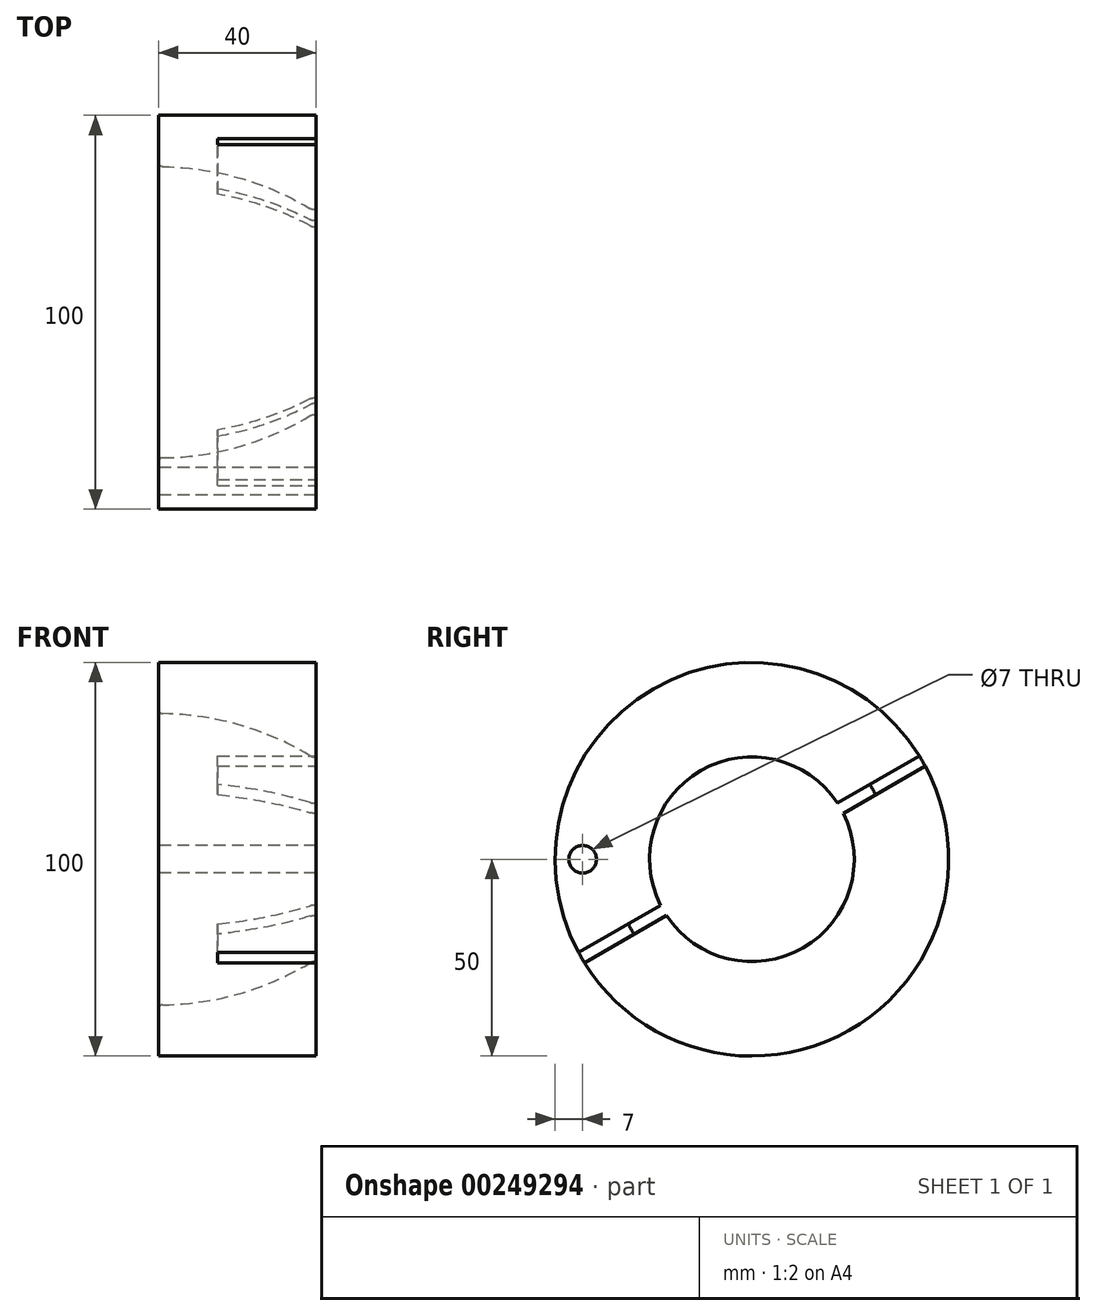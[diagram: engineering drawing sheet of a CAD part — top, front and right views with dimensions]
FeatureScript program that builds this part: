
annotation { "Feature Type Name" : "Feature", "Feature Type Description" : "" }
export const myFeature = defineFeature(function(context is Context, id is Id, definition is map)
    precondition{}
    {
        {
            var Q0;
            Q0=qCreatedBy(makeId("Front.planeOp"),FACE);
            var sketch = newSketch(context, id + "F0", { "sketchPlane" : qUnion([Q0])});
            skLineSegment(sketch, "E0", {"start": v(0, 50) * mm, "end": v(40, 50) * mm});
            skLineSegment(sketch, "E1", {"start": v(0, 0) * mm, "end": v(-40.59, 0) * mm, "construction": true});
            skLineSegment(sketch, "E2", {"start": v(40, 50) * mm, "end": v(40, 26) * mm});
            skLineSegment(sketch, "E3", {"start": v(40, 26) * mm, "end": v(39, 26) * mm});
            skLineSegment(sketch, "E4", {"start": v(0, 50) * mm, "end": v(0, 37) * mm});
            skArc(sketch, "E5", {"start": v(39, 26) * mm, "mid": v(20.26, 34.2) * mm, "end": v(0, 37) * mm});
            skSolve(sketch);
        }
        {
            var Q0;
            Q0=makeQuery(id+"F0.imprint","IMPRINT",FACE,{"disambiguationData":[TD([[makeQuery(id+"F0.imprint","IMPRINT",EDGE,{"derivedFrom":sQuery(id+"F0.wireOp",EDGE,"E0")}),-1.0]])]});
            var Q1;
            Q1=sQuery(id+"F0.wireOp",EDGE,"E1");
            revolve(context, id + "F1", {"surfaceOperationType" : NewSurfaceOperationType.NEW, "entities" : qUnion([Q0]), "axis" : qUnion([Q1]), "revolveType" : RevolveType.FULL});
        }
        {
            var Q0;
            Q0=makeQuery(id+"F1.opRevolve","SWEPT_EDGE",EDGE,{"disambiguationData":[OSD([sQuery(id+"F0.wireOp",EDGE,"E3"),sQuery(id+"F0.wireOp",EDGE,"E5")])]});
            fillet(context, id + "F2", {"entities" : qUnion([Q0]), "tangentPropagation" : true, "radius" : 2 * mm, "defaultsChanged" : true, "vertexSettings" : [], "allowEdgeOverflow" : false});
        }
        {
            var Q0;
            Q0=makeQuery(id+"F1.opRevolve","SWEPT_EDGE",EDGE,{"disambiguationData":[OSD([sQuery(id+"F0.wireOp",EDGE,"E4"),sQuery(id+"F0.wireOp",EDGE,"E5")])]});
            fillet(context, id + "F3", {"entities" : qUnion([Q0]), "tangentPropagation" : true, "radius" : 1 * mm, "defaultsChanged" : false, "vertexSettings" : [], "allowEdgeOverflow" : false});
        }
        {
            var Q0;
            Q0=makeQuery(id+"F1.opRevolve","SWEPT_FACE",FACE,{"disambiguationData":[OSD([sQuery(id+"F0.wireOp",EDGE,"E4")])]});
            var sketch = newSketch(context, id + "F4", { "sketchPlane" : qUnion([Q0])});
            skLineSegment(sketch, "E6", {"start": v(0, 0) * mm, "end": v(43, 0) * mm, "construction": true});
            skCircle(sketch, "E7", {"center": v(43, 0) * mm, "radius": 3.5 * mm});
            skSolve(sketch);
        }
        {
            var Q0;
            Q0=makeQuery(id+"F4.imprint","IMPRINT",FACE,{"disambiguationData":[TD([[makeQuery(id+"F4.imprint","IMPRINT",EDGE,{"derivedFrom":sQuery(id+"F4.wireOp",EDGE,"E7")}),1.0]])]});
            extrude(context, id + "F5", {"entities" : qUnion([Q0]), "operationType" : NewBodyOperationType.REMOVE, "endBound" : BoundingType.THROUGH_ALL, "oppositeDirection" : true, "depth" : 25 * mm, "offsetDistance" : 25 * mm});
        }
        {
            var Q0;
            Q0=makeQuery(id+"F1.opRevolve","SWEPT_FACE",FACE,{"disambiguationData":[OSD([sQuery(id+"F0.wireOp",EDGE,"E2")])]});
            var sketch = newSketch(context, id + "F6", { "sketchPlane" : qUnion([Q0])});
            skLineSegment(sketch, "E8", {"start": v(-52.71, -28.7) * mm, "end": v(51.21, 31.3) * mm});
            skLineSegment(sketch, "E9", {"start": v(51.21, 31.3) * mm, "end": v(52.71, 28.7) * mm});
            skLineSegment(sketch, "E10", {"start": v(52.71, 28.7) * mm, "end": v(-51.21, -31.3) * mm});
            skLineSegment(sketch, "E11", {"start": v(-52.71, -28.7) * mm, "end": v(-51.21, -31.3) * mm});
            skSolve(sketch);
        }
        {
            var Q0;
            {var subQ0=sQuery(id+"F6.wireOp",EDGE,"E8");var subQ1=sQuery(id+"F0.wireOp",EDGE,"E2");var subQ2=makeQuery(id+"F1.opRevolve","SWEPT_EDGE",EDGE,{"disambiguationData":[OSD([sQuery(id+"F0.wireOp",EDGE,"E0"),subQ1])]});var subQ3=makeQuery(id+"F6.imprint","INTERSECT",VERTEX,{"disambiguationData":[OD(1.0)],"derivedFrom":[subQ2,subQ0]});Q0=makeQuery(id+"F6.imprint","IMPRINT",FACE,{"disambiguationData":[TD([[makeQuery(id+"F6.imprint","IMPRINT",EDGE,{"disambiguationData":[TD([[subQ3,1.0]])],"derivedFrom":subQ0}),-1.0]])]});}
            var Q1;
            {var subQ0=sQuery(id+"F6.wireOp",EDGE,"E8");var subQ1=sQuery(id+"F0.wireOp",EDGE,"E2");var subQ2=makeQuery(id+"F1.opRevolve","SWEPT_EDGE",EDGE,{"disambiguationData":[OSD([sQuery(id+"F0.wireOp",EDGE,"E0"),subQ1])]});var subQ3=makeQuery(id+"F6.imprint","INTERSECT",VERTEX,{"disambiguationData":[OD(0.0)],"derivedFrom":[subQ2,subQ0]});Q1=makeQuery(id+"F6.imprint","IMPRINT",FACE,{"disambiguationData":[TD([[makeQuery(id+"F6.imprint","IMPRINT",EDGE,{"disambiguationData":[TD([[subQ3,-1.0]])],"derivedFrom":subQ0}),-1.0]])]});}
            extrude(context, id + "F7", {"entities" : qUnion([Q0, Q1]), "operationType" : NewBodyOperationType.REMOVE, "oppositeDirection" : true, "depth" : 25 * mm, "offsetDistance" : 25 * mm});
        }
    });
